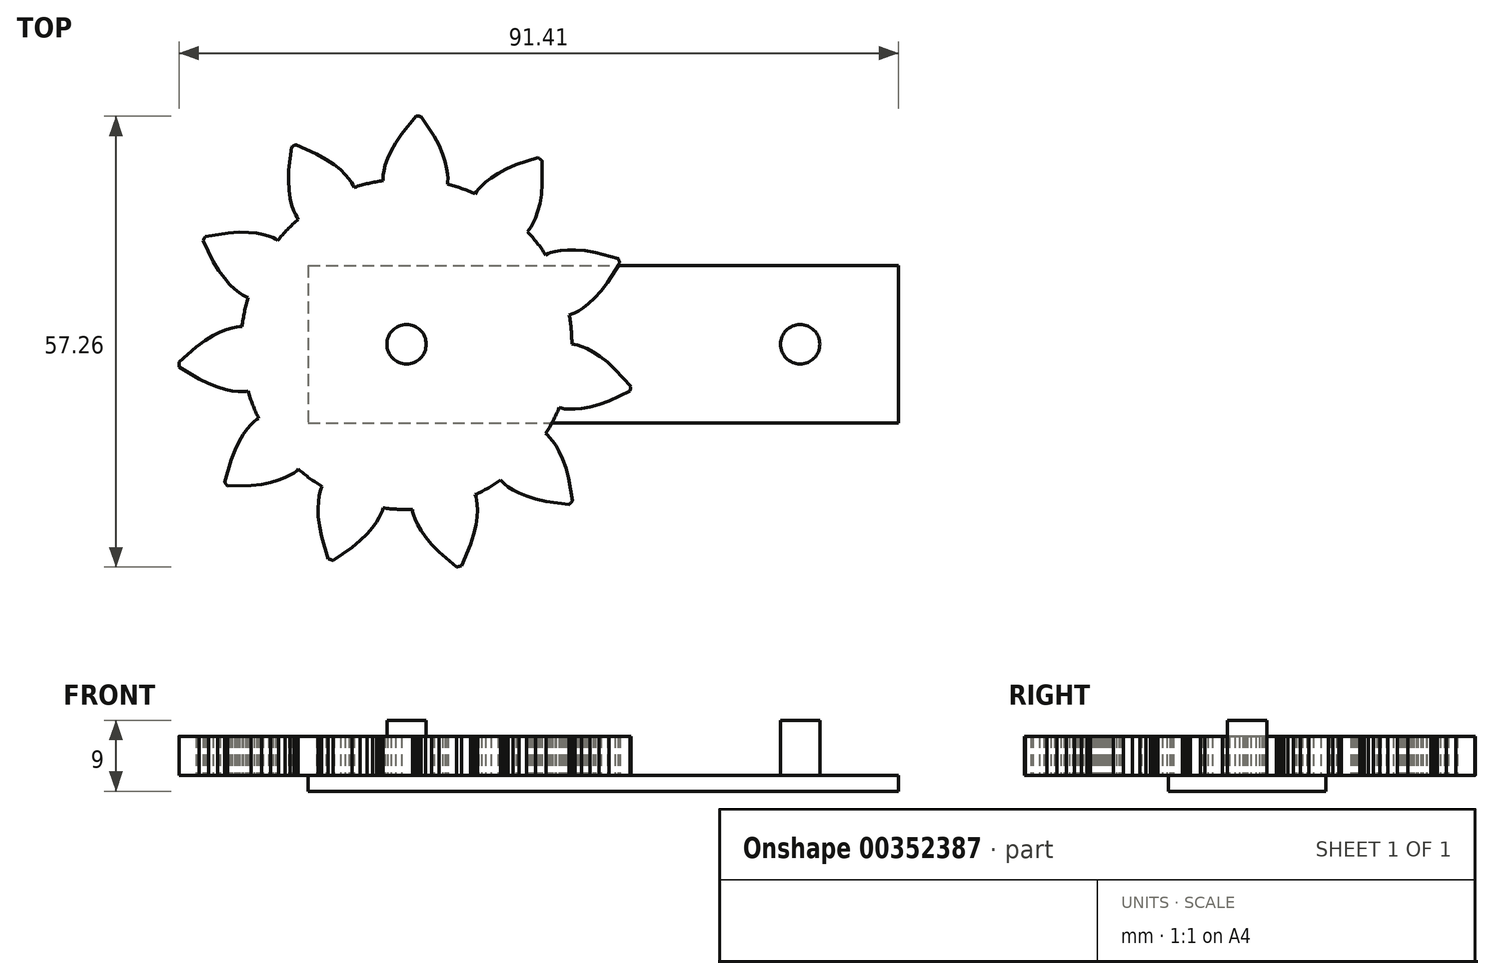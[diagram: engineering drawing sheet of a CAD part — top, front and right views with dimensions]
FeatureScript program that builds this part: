
annotation { "Feature Type Name" : "Feature", "Feature Type Description" : "" }
export const myFeature = defineFeature(function(context is Context, id is Id, definition is map)
    precondition{}
    {
        {
            var Q0;
            Q0=qCreatedBy(makeId("Top.planeOp"),FACE);
            var sketch = newSketch(context, id + "F0", { "sketchPlane" : qUnion([Q0])});
            skCircle(sketch, "E0", {"center": v(0, 0) * mm, "radius": 25 * mm, "construction": true});
            skCircle(sketch, "E1", {"center": v(-50, 0) * mm, "radius": 25 * mm, "construction": true});
            skCircle(sketch, "E2", {"center": v(0, 0) * mm, "radius": 21 * mm, "construction": true});
            skCircle(sketch, "E3", {"center": v(-50, 0) * mm, "radius": 21 * mm, "construction": true});
            skCircle(sketch, "E4", {"center": v(-50, 0) * mm, "radius": 29 * mm, "construction": true});
            skCircle(sketch, "E5", {"center": v(0, 0) * mm, "radius": 29 * mm, "construction": true});
            skLineSegment(sketch, "E6", {"start": v(-32.36, 11.4) * mm, "end": v(-17.64, -11.4) * mm, "construction": true});
            skLineSegment(sketch, "E7", {"start": v(-50, 0) * mm, "end": v(0, 0) * mm, "construction": true});
            skLineSegment(sketch, "E8", {"start": v(-50, 0) * mm, "end": v(-25.48, 4.88) * mm, "construction": true});
            skSolve(sketch);
        }
        {
            var Q0;
            Q0=qCreatedBy(makeId("Top.planeOp"),FACE);
            var sketch = newSketch(context, id + "F1", { "sketchPlane" : qUnion([Q0])});
            skCircle(sketch, "E9.1", {"center": v(-50, 0) * mm, "radius": 25 * mm, "construction": true});
            skCircle(sketch, "E9.2", {"center": v(-50, 0) * mm, "radius": 29 * mm, "construction": true});
            skLineSegment(sketch, "E9.4", {"start": v(-50, 0) * mm, "end": v(-25.48, 4.88) * mm, "construction": true});
            skLineSegment(sketch, "E10", {"start": v(-50, 0) * mm, "end": v(-29, 0) * mm, "construction": true});
            skLineSegment(sketch, "E11.1.0", {"start": v(-50, 0) * mm, "end": v(-29.08, -1.83) * mm, "construction": true});
            skLineSegment(sketch, "E11.2.0", {"start": v(-50, 0) * mm, "end": v(-29.32, -3.65) * mm, "construction": true});
            skLineSegment(sketch, "E11.3.0", {"start": v(-50, 0) * mm, "end": v(-29.72, -5.44) * mm, "construction": true});
            skLineSegment(sketch, "E11.4.0", {"start": v(-50, 0) * mm, "end": v(-30.27, -7.18) * mm, "construction": true});
            skLineSegment(sketch, "E11.5.0", {"start": v(-50, 0) * mm, "end": v(-30.97, -8.87) * mm, "construction": true});
            skLineSegment(sketch, "E11.6.0", {"start": v(-50, 0) * mm, "end": v(-31.81, -10.5) * mm, "construction": true});
            skLineSegment(sketch, "E11.7.0", {"start": v(-50, 0) * mm, "end": v(-32.8, -12.05) * mm, "construction": true});
            skLineSegment(sketch, "E11.8.0", {"start": v(-50, 0) * mm, "end": v(-33.91, -13.5) * mm, "construction": true});
            skLineSegment(sketch, "E11.9.0", {"start": v(-50, 0) * mm, "end": v(-35.15, -14.85) * mm, "construction": true});
            skLineSegment(sketch, "E11.10.0", {"start": v(-50, 0) * mm, "end": v(-36.5, -16.09) * mm, "construction": true});
            skLineSegment(sketch, "E11.anchor2", {"start": v(-50, 0) * mm, "end": v(-36.5, -16.09) * mm, "construction": true});
            skArc(sketch, "E12", {"start": v(-29.08, -1.83) * mm, "mid": v(-29.02, -0.92) * mm, "end": v(-29, 0) * mm, "construction": true});
            skArc(sketch, "E13", {"start": v(-29, 0) * mm, "mid": v(-70.98, 0.92) * mm, "end": v(-29.08, -1.83) * mm, "construction": true});
            skLineSegment(sketch, "E14", {"start": v(-29.32, -3.65) * mm, "end": v(-28.68, -0.04) * mm, "construction": true});
            skLineSegment(sketch, "E15", {"start": v(-29.72, -5.44) * mm, "end": v(-28.3, -0.12) * mm, "construction": true});
            skLineSegment(sketch, "E16", {"start": v(-30.27, -7.18) * mm, "end": v(-27.76, -0.3) * mm, "construction": true});
            skLineSegment(sketch, "E17", {"start": v(-30.97, -8.87) * mm, "end": v(-27.1, -0.57) * mm, "construction": true});
            skLineSegment(sketch, "E18", {"start": v(-31.81, -10.5) * mm, "end": v(-26.31, -0.98) * mm, "construction": true});
            skLineSegment(sketch, "E19", {"start": v(-32.8, -12.05) * mm, "end": v(-25.44, -1.53) * mm, "construction": true});
            skLineSegment(sketch, "E20", {"start": v(-33.91, -13.5) * mm, "end": v(-24.49, -2.27) * mm, "construction": true});
            skLineSegment(sketch, "E21", {"start": v(-35.15, -14.85) * mm, "end": v(-23.49, -3.18) * mm, "construction": true});
            skLineSegment(sketch, "E22", {"start": v(-36.5, -16.09) * mm, "end": v(-22.46, -4.3) * mm, "construction": true});
            skLineSegment(sketch, "E23", {"start": v(-29, 0) * mm, "end": v(-28.68, -0.04) * mm});
            skLineSegment(sketch, "E24", {"start": v(-28.68, -0.04) * mm, "end": v(-28.3, -0.12) * mm});
            skLineSegment(sketch, "E25", {"start": v(-28.3, -0.12) * mm, "end": v(-27.76, -0.3) * mm});
            skLineSegment(sketch, "E26", {"start": v(-27.76, -0.3) * mm, "end": v(-27.1, -0.57) * mm});
            skLineSegment(sketch, "E27", {"start": v(-27.1, -0.57) * mm, "end": v(-26.31, -0.98) * mm});
            skLineSegment(sketch, "E28", {"start": v(-26.31, -0.98) * mm, "end": v(-25.44, -1.53) * mm});
            skLineSegment(sketch, "E29", {"start": v(-25.44, -1.53) * mm, "end": v(-24.49, -2.27) * mm});
            skLineSegment(sketch, "E30", {"start": v(-24.49, -2.27) * mm, "end": v(-23.49, -3.18) * mm});
            skLineSegment(sketch, "E31", {"start": v(-23.49, -3.18) * mm, "end": v(-21.5, -5.35) * mm});
            skSolve(sketch);
        }
        {
            var Q0;
            Q0=qCreatedBy(makeId("Top.planeOp"),FACE);
            var sketch = newSketch(context, id + "F2", { "sketchPlane" : qUnion([Q0])});
            skLineSegment(sketch, "E32.0", {"start": v(-50, 0) * mm, "end": v(-29, 0) * mm, "construction": true});
            skLineSegment(sketch, "E32.1", {"start": v(-29, 0) * mm, "end": v(-28.68, -0.04) * mm});
            skLineSegment(sketch, "E32.2", {"start": v(-28.68, -0.04) * mm, "end": v(-28.3, -0.12) * mm});
            skLineSegment(sketch, "E32.3", {"start": v(-28.3, -0.12) * mm, "end": v(-27.76, -0.3) * mm});
            skLineSegment(sketch, "E32.4", {"start": v(-27.76, -0.3) * mm, "end": v(-27.1, -0.57) * mm});
            skLineSegment(sketch, "E32.5", {"start": v(-27.1, -0.57) * mm, "end": v(-26.31, -0.98) * mm});
            skLineSegment(sketch, "E32.6", {"start": v(-26.31, -0.98) * mm, "end": v(-25.44, -1.53) * mm});
            skLineSegment(sketch, "E32.7", {"start": v(-25.44, -1.53) * mm, "end": v(-24.49, -2.27) * mm});
            skArc(sketch, "E32.9", {"start": v(-21.56, -5.66) * mm, "mid": v(-21.53, -5.5) * mm, "end": v(-21.5, -5.35) * mm});
            skArc(sketch, "E33.converted", {"start": v(-29, 0) * mm, "mid": v(-29.1, 2.06) * mm, "end": v(-29.4, 4.1) * mm});
            skLineSegment(sketch, "E34", {"start": v(-50, 0) * mm, "end": v(-21.56, -5.66) * mm, "construction": true});
            skLineSegment(sketch, "E35", {"start": v(-50, 0) * mm, "end": v(-21.56, 5.66) * mm, "construction": true});
            skCircle(sketch, "E36", {"center": v(-50, 0) * mm, "radius": 2.5 * mm});
            skPoint(sketch, "E37", {"position": v(-29.1, 2.06) * mm});
            skLineSegment(sketch, "E38.0", {"start": v(-23.49, -3.18) * mm, "end": v(-21.5, -5.35) * mm});
            skLineSegment(sketch, "E38.1", {"start": v(-24.49, -2.27) * mm, "end": v(-23.49, -3.18) * mm});
            skPoint(sketch, "E38.2", {"position": v(-23.99, -2.72) * mm});
            skArc(sketch, "E39.MirrorCS", {"start": v(-21.56, -5.66) * mm, "mid": v(-21.59, -5.8) * mm, "end": v(-21.62, -5.96) * mm});
            skLineSegment(sketch, "E40.MirrorCS", {"start": v(-24.29, -7.2) * mm, "end": v(-21.62, -5.96) * mm});
            skLineSegment(sketch, "E41.MirrorCS", {"start": v(-25.56, -7.67) * mm, "end": v(-24.29, -7.2) * mm});
            skLineSegment(sketch, "E42.MirrorCS", {"start": v(-26.72, -7.98) * mm, "end": v(-25.56, -7.67) * mm});
            skLineSegment(sketch, "E43.MirrorCS", {"start": v(-27.74, -8.16) * mm, "end": v(-26.72, -7.98) * mm});
            skLineSegment(sketch, "E44.MirrorCS", {"start": v(-29.34, -8.24) * mm, "end": v(-28.62, -8.24) * mm});
            skLineSegment(sketch, "E45.MirrorCS", {"start": v(-28.62, -8.24) * mm, "end": v(-27.74, -8.16) * mm});
            skLineSegment(sketch, "E46.MirrorCS", {"start": v(-29.9, -8.2) * mm, "end": v(-29.34, -8.24) * mm});
            skLineSegment(sketch, "E47.MirrorCS", {"start": v(-30.3, -8.12) * mm, "end": v(-29.9, -8.2) * mm});
            skLineSegment(sketch, "E48.MirrorCS", {"start": v(-30.6, -8.04) * mm, "end": v(-30.3, -8.12) * mm});
            skArc(sketch, "E49.MirrorCS", {"start": v(-30.6, -8.04) * mm, "mid": v(-31.48, -9.9) * mm, "end": v(-32.54, -11.67) * mm});
            skArc(sketch, "E50.1.0", {"start": v(-29.33, 3.73) * mm, "mid": v(-29.07, 1.69) * mm, "end": v(-29, -0.37) * mm});
            skArc(sketch, "E50.1.1", {"start": v(-32.33, 11.35) * mm, "mid": v(-33.53, 13.03) * mm, "end": v(-34.89, 14.58) * mm});
            skLineSegment(sketch, "E50.1.2", {"start": v(-32.33, 11.35) * mm, "end": v(-32.05, 11.5) * mm});
            skLineSegment(sketch, "E50.1.3", {"start": v(-32.05, 11.5) * mm, "end": v(-31.67, 11.63) * mm});
            skLineSegment(sketch, "E50.1.4", {"start": v(-31.67, 11.63) * mm, "end": v(-31.13, 11.78) * mm});
            skLineSegment(sketch, "E50.1.5", {"start": v(-31.13, 11.78) * mm, "end": v(-30.42, 11.9) * mm});
            skLineSegment(sketch, "E50.1.6", {"start": v(-30.42, 11.9) * mm, "end": v(-29.55, 11.98) * mm});
            skLineSegment(sketch, "E50.1.7", {"start": v(-29.55, 11.98) * mm, "end": v(-28.5, 11.99) * mm});
            skLineSegment(sketch, "E50.1.8", {"start": v(-28.5, 11.99) * mm, "end": v(-27.31, 11.89) * mm});
            skLineSegment(sketch, "E50.1.9", {"start": v(-27.31, 11.89) * mm, "end": v(-25.97, 11.66) * mm});
            skLineSegment(sketch, "E50.1.10", {"start": v(-25.97, 11.66) * mm, "end": v(-23.13, 10.9) * mm});
            skArc(sketch, "E50.1.11", {"start": v(-23.01, 10.62) * mm, "mid": v(-23.07, 10.76) * mm, "end": v(-23.13, 10.9) * mm});
            skArc(sketch, "E50.1.12", {"start": v(-23.01, 10.62) * mm, "mid": v(-22.96, 10.47) * mm, "end": v(-22.9, 10.33) * mm});
            skLineSegment(sketch, "E50.1.13", {"start": v(-24.47, 7.84) * mm, "end": v(-22.9, 10.33) * mm});
            skLineSegment(sketch, "E50.1.14", {"start": v(-25.3, 6.76) * mm, "end": v(-24.47, 7.84) * mm});
            skLineSegment(sketch, "E50.1.15", {"start": v(-26.1, 5.87) * mm, "end": v(-25.3, 6.76) * mm});
            skLineSegment(sketch, "E50.1.16", {"start": v(-26.86, 5.17) * mm, "end": v(-26.1, 5.87) * mm});
            skLineSegment(sketch, "E50.1.17", {"start": v(-27.56, 4.63) * mm, "end": v(-26.86, 5.17) * mm});
            skLineSegment(sketch, "E50.1.18", {"start": v(-28.16, 4.24) * mm, "end": v(-27.56, 4.63) * mm});
            skLineSegment(sketch, "E50.1.19", {"start": v(-28.66, 3.98) * mm, "end": v(-28.16, 4.24) * mm});
            skLineSegment(sketch, "E50.1.20", {"start": v(-29.03, 3.82) * mm, "end": v(-28.66, 3.98) * mm});
            skLineSegment(sketch, "E50.1.21", {"start": v(-29.33, 3.73) * mm, "end": v(-29.03, 3.82) * mm});
            skArc(sketch, "E50.2.0", {"start": v(-34.63, 14.3) * mm, "mid": v(-33.3, 12.73) * mm, "end": v(-32.13, 11.04) * mm});
            skArc(sketch, "E50.2.1", {"start": v(-41.28, 19.1) * mm, "mid": v(-43.2, 19.87) * mm, "end": v(-45.17, 20.44) * mm});
            skLineSegment(sketch, "E50.2.2", {"start": v(-41.28, 19.1) * mm, "end": v(-41.11, 19.38) * mm});
            skLineSegment(sketch, "E50.2.3", {"start": v(-41.11, 19.38) * mm, "end": v(-40.87, 19.7) * mm});
            skLineSegment(sketch, "E50.2.4", {"start": v(-40.87, 19.7) * mm, "end": v(-40.5, 20.1) * mm});
            skLineSegment(sketch, "E50.2.5", {"start": v(-40.5, 20.1) * mm, "end": v(-39.97, 20.6) * mm});
            skLineSegment(sketch, "E50.2.6", {"start": v(-39.97, 20.6) * mm, "end": v(-39.27, 21.14) * mm});
            skLineSegment(sketch, "E50.2.7", {"start": v(-39.27, 21.14) * mm, "end": v(-38.4, 21.7) * mm});
            skLineSegment(sketch, "E50.2.8", {"start": v(-38.4, 21.7) * mm, "end": v(-37.34, 22.27) * mm});
            skLineSegment(sketch, "E50.2.9", {"start": v(-37.34, 22.27) * mm, "end": v(-36.09, 22.8) * mm});
            skLineSegment(sketch, "E50.2.10", {"start": v(-36.09, 22.8) * mm, "end": v(-33.29, 23.7) * mm});
            skArc(sketch, "E50.2.11", {"start": v(-33.04, 23.52) * mm, "mid": v(-33.16, 23.61) * mm, "end": v(-33.29, 23.7) * mm});
            skArc(sketch, "E50.2.12", {"start": v(-33.04, 23.52) * mm, "mid": v(-32.91, 23.43) * mm, "end": v(-32.79, 23.34) * mm});
            skLineSegment(sketch, "E50.2.13", {"start": v(-32.76, 20.4) * mm, "end": v(-32.79, 23.34) * mm});
            skLineSegment(sketch, "E50.2.14", {"start": v(-32.87, 19.04) * mm, "end": v(-32.76, 20.4) * mm});
            skLineSegment(sketch, "E50.2.15", {"start": v(-33.07, 17.86) * mm, "end": v(-32.87, 19.04) * mm});
            skLineSegment(sketch, "E50.2.16", {"start": v(-33.33, 16.85) * mm, "end": v(-33.07, 17.86) * mm});
            skLineSegment(sketch, "E50.2.17", {"start": v(-33.62, 16.02) * mm, "end": v(-33.33, 16.85) * mm});
            skLineSegment(sketch, "E50.2.18", {"start": v(-33.92, 15.37) * mm, "end": v(-33.62, 16.02) * mm});
            skLineSegment(sketch, "E50.2.19", {"start": v(-34.2, 14.88) * mm, "end": v(-33.92, 15.37) * mm});
            skLineSegment(sketch, "E50.2.20", {"start": v(-34.42, 14.55) * mm, "end": v(-34.2, 14.88) * mm});
            skLineSegment(sketch, "E50.2.21", {"start": v(-34.63, 14.3) * mm, "end": v(-34.42, 14.55) * mm});
            skArc(sketch, "E50.3.0", {"start": v(-44.8, 20.35) * mm, "mid": v(-42.84, 19.74) * mm, "end": v(-40.94, 18.94) * mm});
            skArc(sketch, "E50.3.1", {"start": v(-52.99, 20.79) * mm, "mid": v(-55.01, 20.4) * mm, "end": v(-56.99, 19.8) * mm});
            skLineSegment(sketch, "E50.3.2", {"start": v(-52.99, 20.79) * mm, "end": v(-53, 21.1) * mm});
            skLineSegment(sketch, "E50.3.3", {"start": v(-53, 21.1) * mm, "end": v(-52.97, 21.5) * mm});
            skLineSegment(sketch, "E50.3.4", {"start": v(-52.97, 21.5) * mm, "end": v(-52.88, 22.06) * mm});
            skLineSegment(sketch, "E50.3.5", {"start": v(-52.88, 22.06) * mm, "end": v(-52.7, 22.75) * mm});
            skLineSegment(sketch, "E50.3.6", {"start": v(-52.7, 22.75) * mm, "end": v(-52.4, 23.58) * mm});
            skLineSegment(sketch, "E50.3.7", {"start": v(-52.4, 23.58) * mm, "end": v(-51.98, 24.53) * mm});
            skLineSegment(sketch, "E50.3.8", {"start": v(-51.98, 24.53) * mm, "end": v(-51.39, 25.58) * mm});
            skLineSegment(sketch, "E50.3.9", {"start": v(-51.39, 25.58) * mm, "end": v(-50.62, 26.7) * mm});
            skLineSegment(sketch, "E50.3.10", {"start": v(-50.62, 26.7) * mm, "end": v(-48.76, 28.97) * mm});
            skArc(sketch, "E50.3.11", {"start": v(-48.45, 28.96) * mm, "mid": v(-48.6, 28.97) * mm, "end": v(-48.76, 28.97) * mm});
            skArc(sketch, "E50.3.12", {"start": v(-48.45, 28.96) * mm, "mid": v(-48.3, 28.95) * mm, "end": v(-48.14, 28.94) * mm});
            skLineSegment(sketch, "E50.3.13", {"start": v(-46.53, 26.48) * mm, "end": v(-48.14, 28.94) * mm});
            skLineSegment(sketch, "E50.3.14", {"start": v(-45.89, 25.28) * mm, "end": v(-46.53, 26.48) * mm});
            skLineSegment(sketch, "E50.3.15", {"start": v(-45.41, 24.18) * mm, "end": v(-45.89, 25.28) * mm});
            skLineSegment(sketch, "E50.3.16", {"start": v(-45.09, 23.2) * mm, "end": v(-45.41, 24.18) * mm});
            skLineSegment(sketch, "E50.3.17", {"start": v(-44.89, 22.33) * mm, "end": v(-45.09, 23.2) * mm});
            skLineSegment(sketch, "E50.3.18", {"start": v(-44.78, 21.62) * mm, "end": v(-44.89, 22.33) * mm});
            skLineSegment(sketch, "E50.3.19", {"start": v(-44.75, 21.06) * mm, "end": v(-44.78, 21.62) * mm});
            skLineSegment(sketch, "E50.3.20", {"start": v(-44.76, 20.66) * mm, "end": v(-44.75, 21.06) * mm});
            skLineSegment(sketch, "E50.3.21", {"start": v(-44.8, 20.35) * mm, "end": v(-44.76, 20.66) * mm});
            skArc(sketch, "E50.4.0", {"start": v(-56.63, 19.93) * mm, "mid": v(-54.65, 20.48) * mm, "end": v(-52.62, 20.84) * mm});
            skArc(sketch, "E50.4.1", {"start": v(-63.75, 15.87) * mm, "mid": v(-65.24, 14.45) * mm, "end": v(-66.58, 12.88) * mm});
            skLineSegment(sketch, "E50.4.2", {"start": v(-63.75, 15.87) * mm, "end": v(-63.93, 16.13) * mm});
            skLineSegment(sketch, "E50.4.3", {"start": v(-63.93, 16.13) * mm, "end": v(-64.12, 16.49) * mm});
            skLineSegment(sketch, "E50.4.4", {"start": v(-64.12, 16.49) * mm, "end": v(-64.34, 17) * mm});
            skLineSegment(sketch, "E50.4.5", {"start": v(-64.34, 17) * mm, "end": v(-64.57, 17.68) * mm});
            skLineSegment(sketch, "E50.4.6", {"start": v(-64.57, 17.68) * mm, "end": v(-64.77, 18.54) * mm});
            skLineSegment(sketch, "E50.4.7", {"start": v(-64.77, 18.54) * mm, "end": v(-64.92, 19.57) * mm});
            skLineSegment(sketch, "E50.4.8", {"start": v(-64.92, 19.57) * mm, "end": v(-65, 20.76) * mm});
            skLineSegment(sketch, "E50.4.9", {"start": v(-65, 20.76) * mm, "end": v(-64.96, 22.12) * mm});
            skLineSegment(sketch, "E50.4.10", {"start": v(-64.96, 22.12) * mm, "end": v(-64.62, 25.05) * mm});
            skArc(sketch, "E50.4.11", {"start": v(-64.35, 25.2) * mm, "mid": v(-64.48, 25.12) * mm, "end": v(-64.62, 25.05) * mm});
            skArc(sketch, "E50.4.12", {"start": v(-64.35, 25.2) * mm, "mid": v(-64.22, 25.28) * mm, "end": v(-64.08, 25.35) * mm});
            skLineSegment(sketch, "E50.4.13", {"start": v(-61.4, 24.15) * mm, "end": v(-64.08, 25.35) * mm});
            skLineSegment(sketch, "E50.4.14", {"start": v(-60.2, 23.5) * mm, "end": v(-61.4, 24.15) * mm});
            skLineSegment(sketch, "E50.4.15", {"start": v(-59.21, 22.82) * mm, "end": v(-60.2, 23.5) * mm});
            skLineSegment(sketch, "E50.4.16", {"start": v(-58.4, 22.17) * mm, "end": v(-59.21, 22.82) * mm});
            skLineSegment(sketch, "E50.4.17", {"start": v(-57.77, 21.55) * mm, "end": v(-58.4, 22.17) * mm});
            skLineSegment(sketch, "E50.4.18", {"start": v(-57.3, 21.01) * mm, "end": v(-57.77, 21.55) * mm});
            skLineSegment(sketch, "E50.4.19", {"start": v(-56.97, 20.56) * mm, "end": v(-57.3, 21.01) * mm});
            skLineSegment(sketch, "E50.4.20", {"start": v(-56.77, 20.22) * mm, "end": v(-56.97, 20.56) * mm});
            skLineSegment(sketch, "E50.4.21", {"start": v(-56.63, 19.93) * mm, "end": v(-56.77, 20.22) * mm});
            skArc(sketch, "E50.5.0", {"start": v(-66.35, 13.18) * mm, "mid": v(-64.98, 14.72) * mm, "end": v(-63.47, 16.11) * mm});
            skArc(sketch, "E50.5.1", {"start": v(-70.15, 5.92) * mm, "mid": v(-70.63, 3.91) * mm, "end": v(-70.92, 1.87) * mm});
            skLineSegment(sketch, "E50.5.2", {"start": v(-70.15, 5.92) * mm, "end": v(-70.44, 6.04) * mm});
            skLineSegment(sketch, "E50.5.3", {"start": v(-70.44, 6.04) * mm, "end": v(-70.8, 6.23) * mm});
            skLineSegment(sketch, "E50.5.4", {"start": v(-70.8, 6.23) * mm, "end": v(-71.26, 6.55) * mm});
            skLineSegment(sketch, "E50.5.5", {"start": v(-71.26, 6.55) * mm, "end": v(-71.82, 7) * mm});
            skLineSegment(sketch, "E50.5.6", {"start": v(-71.82, 7) * mm, "end": v(-72.45, 7.6) * mm});
            skLineSegment(sketch, "E50.5.7", {"start": v(-72.45, 7.6) * mm, "end": v(-73.13, 8.4) * mm});
            skLineSegment(sketch, "E50.5.8", {"start": v(-73.13, 8.4) * mm, "end": v(-73.84, 9.36) * mm});
            skLineSegment(sketch, "E50.5.9", {"start": v(-73.84, 9.36) * mm, "end": v(-74.54, 10.53) * mm});
            skLineSegment(sketch, "E50.5.10", {"start": v(-74.54, 10.53) * mm, "end": v(-75.84, 13.17) * mm});
            skArc(sketch, "E50.5.11", {"start": v(-75.7, 13.44) * mm, "mid": v(-75.77, 13.3) * mm, "end": v(-75.84, 13.17) * mm});
            skArc(sketch, "E50.5.12", {"start": v(-75.7, 13.44) * mm, "mid": v(-75.62, 13.58) * mm, "end": v(-75.55, 13.71) * mm});
            skLineSegment(sketch, "E50.5.13", {"start": v(-72.64, 14.16) * mm, "end": v(-75.55, 13.71) * mm});
            skLineSegment(sketch, "E50.5.14", {"start": v(-71.29, 14.24) * mm, "end": v(-72.64, 14.16) * mm});
            skLineSegment(sketch, "E50.5.15", {"start": v(-70.09, 14.22) * mm, "end": v(-71.29, 14.24) * mm});
            skLineSegment(sketch, "E50.5.16", {"start": v(-69.05, 14.1) * mm, "end": v(-70.09, 14.22) * mm});
            skLineSegment(sketch, "E50.5.17", {"start": v(-68.2, 13.93) * mm, "end": v(-69.05, 14.1) * mm});
            skLineSegment(sketch, "E50.5.18", {"start": v(-67.5, 13.73) * mm, "end": v(-68.2, 13.93) * mm});
            skLineSegment(sketch, "E50.5.19", {"start": v(-66.98, 13.52) * mm, "end": v(-67.5, 13.73) * mm});
            skLineSegment(sketch, "E50.5.20", {"start": v(-66.62, 13.35) * mm, "end": v(-66.98, 13.52) * mm});
            skLineSegment(sketch, "E50.5.21", {"start": v(-66.35, 13.18) * mm, "end": v(-66.62, 13.35) * mm});
            skArc(sketch, "E50.6.0", {"start": v(-70.88, 2.24) * mm, "mid": v(-70.56, 4.28) * mm, "end": v(-70.04, 6.28) * mm});
            skArc(sketch, "E50.6.1", {"start": v(-70.15, -5.92) * mm, "mid": v(-69.47, -7.86) * mm, "end": v(-68.6, -9.73) * mm});
            skLineSegment(sketch, "E50.6.2", {"start": v(-70.15, -5.92) * mm, "end": v(-70.46, -5.97) * mm});
            skLineSegment(sketch, "E50.6.3", {"start": v(-70.46, -5.97) * mm, "end": v(-70.86, -6) * mm});
            skLineSegment(sketch, "E50.6.4", {"start": v(-70.86, -6) * mm, "end": v(-71.42, -5.99) * mm});
            skLineSegment(sketch, "E50.6.5", {"start": v(-71.42, -5.99) * mm, "end": v(-72.14, -5.9) * mm});
            skLineSegment(sketch, "E50.6.6", {"start": v(-72.14, -5.9) * mm, "end": v(-73, -5.74) * mm});
            skLineSegment(sketch, "E50.6.7", {"start": v(-73, -5.74) * mm, "end": v(-74, -5.45) * mm});
            skLineSegment(sketch, "E50.6.8", {"start": v(-74, -5.45) * mm, "end": v(-75.12, -5.01) * mm});
            skLineSegment(sketch, "E50.6.9", {"start": v(-75.12, -5.01) * mm, "end": v(-76.34, -4.41) * mm});
            skLineSegment(sketch, "E50.6.10", {"start": v(-76.34, -4.41) * mm, "end": v(-78.86, -2.9) * mm});
            skArc(sketch, "E50.6.11", {"start": v(-78.88, -2.58) * mm, "mid": v(-78.87, -2.74) * mm, "end": v(-78.86, -2.9) * mm});
            skArc(sketch, "E50.6.12", {"start": v(-78.88, -2.58) * mm, "mid": v(-78.9, -2.43) * mm, "end": v(-78.91, -2.28) * mm});
            skLineSegment(sketch, "E50.6.13", {"start": v(-76.7, -0.33) * mm, "end": v(-78.91, -2.28) * mm});
            skLineSegment(sketch, "E50.6.14", {"start": v(-75.6, 0.47) * mm, "end": v(-76.7, -0.33) * mm});
            skLineSegment(sketch, "E50.6.15", {"start": v(-74.59, 1.1) * mm, "end": v(-75.6, 0.47) * mm});
            skLineSegment(sketch, "E50.6.16", {"start": v(-73.65, 1.56) * mm, "end": v(-74.59, 1.1) * mm});
            skLineSegment(sketch, "E50.6.17", {"start": v(-72.84, 1.88) * mm, "end": v(-73.65, 1.56) * mm});
            skLineSegment(sketch, "E50.6.18", {"start": v(-72.15, 2.09) * mm, "end": v(-72.84, 1.88) * mm});
            skLineSegment(sketch, "E50.6.19", {"start": v(-71.6, 2.2) * mm, "end": v(-72.15, 2.09) * mm});
            skLineSegment(sketch, "E50.6.20", {"start": v(-71.2, 2.24) * mm, "end": v(-71.6, 2.2) * mm});
            skLineSegment(sketch, "E50.6.21", {"start": v(-70.88, 2.24) * mm, "end": v(-71.2, 2.24) * mm});
            skArc(sketch, "E50.7.0", {"start": v(-68.78, -9.4) * mm, "mid": v(-69.6, -7.51) * mm, "end": v(-70.25, -5.56) * mm});
            skArc(sketch, "E50.7.1", {"start": v(-63.75, -15.87) * mm, "mid": v(-62.13, -17.14) * mm, "end": v(-60.4, -18.25) * mm});
            skLineSegment(sketch, "E50.7.2", {"start": v(-63.75, -15.87) * mm, "end": v(-63.99, -16.09) * mm});
            skLineSegment(sketch, "E50.7.3", {"start": v(-63.99, -16.09) * mm, "end": v(-64.3, -16.32) * mm});
            skLineSegment(sketch, "E50.7.4", {"start": v(-64.3, -16.32) * mm, "end": v(-64.79, -16.62) * mm});
            skLineSegment(sketch, "E50.7.5", {"start": v(-64.79, -16.62) * mm, "end": v(-65.43, -16.94) * mm});
            skLineSegment(sketch, "E50.7.6", {"start": v(-65.43, -16.94) * mm, "end": v(-66.25, -17.26) * mm});
            skLineSegment(sketch, "E50.7.7", {"start": v(-66.25, -17.26) * mm, "end": v(-67.24, -17.56) * mm});
            skLineSegment(sketch, "E50.7.8", {"start": v(-67.24, -17.56) * mm, "end": v(-68.42, -17.8) * mm});
            skLineSegment(sketch, "E50.7.9", {"start": v(-68.42, -17.8) * mm, "end": v(-69.77, -17.95) * mm});
            skLineSegment(sketch, "E50.7.10", {"start": v(-69.77, -17.95) * mm, "end": v(-72.71, -18.03) * mm});
            skArc(sketch, "E50.7.11", {"start": v(-72.9, -17.8) * mm, "mid": v(-72.8, -17.91) * mm, "end": v(-72.71, -18.03) * mm});
            skArc(sketch, "E50.7.12", {"start": v(-72.9, -17.8) * mm, "mid": v(-73, -17.67) * mm, "end": v(-73.09, -17.55) * mm});
            skLineSegment(sketch, "E50.7.13", {"start": v(-72.28, -14.72) * mm, "end": v(-73.09, -17.55) * mm});
            skLineSegment(sketch, "E50.7.14", {"start": v(-71.8, -13.45) * mm, "end": v(-72.28, -14.72) * mm});
            skLineSegment(sketch, "E50.7.15", {"start": v(-71.28, -12.37) * mm, "end": v(-71.8, -13.45) * mm});
            skLineSegment(sketch, "E50.7.16", {"start": v(-70.74, -11.47) * mm, "end": v(-71.28, -12.37) * mm});
            skLineSegment(sketch, "E50.7.17", {"start": v(-70.23, -10.76) * mm, "end": v(-70.74, -11.47) * mm});
            skLineSegment(sketch, "E50.7.18", {"start": v(-69.76, -10.22) * mm, "end": v(-70.23, -10.76) * mm});
            skLineSegment(sketch, "E50.7.19", {"start": v(-69.36, -9.83) * mm, "end": v(-69.76, -10.22) * mm});
            skLineSegment(sketch, "E50.7.20", {"start": v(-69.05, -9.57) * mm, "end": v(-69.36, -9.83) * mm});
            skLineSegment(sketch, "E50.7.21", {"start": v(-68.78, -9.4) * mm, "end": v(-69.05, -9.57) * mm});
            skArc(sketch, "E50.8.0", {"start": v(-60.72, -18.06) * mm, "mid": v(-62.43, -16.92) * mm, "end": v(-64.03, -15.62) * mm});
            skArc(sketch, "E50.8.1", {"start": v(-52.99, -20.79) * mm, "mid": v(-50.94, -20.98) * mm, "end": v(-48.88, -20.97) * mm});
            skLineSegment(sketch, "E50.8.2", {"start": v(-52.99, -20.79) * mm, "end": v(-53.07, -21.1) * mm});
            skLineSegment(sketch, "E50.8.3", {"start": v(-53.07, -21.1) * mm, "end": v(-53.21, -21.47) * mm});
            skLineSegment(sketch, "E50.8.4", {"start": v(-53.21, -21.47) * mm, "end": v(-53.45, -21.97) * mm});
            skLineSegment(sketch, "E50.8.5", {"start": v(-53.45, -21.97) * mm, "end": v(-53.82, -22.6) * mm});
            skLineSegment(sketch, "E50.8.6", {"start": v(-53.82, -22.6) * mm, "end": v(-54.34, -23.3) * mm});
            skLineSegment(sketch, "E50.8.7", {"start": v(-54.34, -23.3) * mm, "end": v(-55.01, -24.1) * mm});
            skLineSegment(sketch, "E50.8.8", {"start": v(-55.01, -24.1) * mm, "end": v(-55.87, -24.93) * mm});
            skLineSegment(sketch, "E50.8.9", {"start": v(-55.87, -24.93) * mm, "end": v(-56.93, -25.8) * mm});
            skLineSegment(sketch, "E50.8.10", {"start": v(-56.93, -25.8) * mm, "end": v(-59.36, -27.45) * mm});
            skArc(sketch, "E50.8.11", {"start": v(-59.65, -27.35) * mm, "mid": v(-59.5, -27.4) * mm, "end": v(-59.36, -27.45) * mm});
            skArc(sketch, "E50.8.12", {"start": v(-59.65, -27.35) * mm, "mid": v(-59.8, -27.3) * mm, "end": v(-59.94, -27.24) * mm});
            skLineSegment(sketch, "E50.8.13", {"start": v(-60.8, -24.43) * mm, "end": v(-59.94, -27.24) * mm});
            skLineSegment(sketch, "E50.8.14", {"start": v(-61.07, -23.1) * mm, "end": v(-60.8, -24.43) * mm});
            skLineSegment(sketch, "E50.8.15", {"start": v(-61.21, -21.9) * mm, "end": v(-61.07, -23.1) * mm});
            skLineSegment(sketch, "E50.8.16", {"start": v(-61.25, -20.87) * mm, "end": v(-61.21, -21.9) * mm});
            skLineSegment(sketch, "E50.8.17", {"start": v(-61.2, -19.99) * mm, "end": v(-61.25, -20.87) * mm});
            skLineSegment(sketch, "E50.8.18", {"start": v(-61.1, -19.28) * mm, "end": v(-61.2, -19.99) * mm});
            skLineSegment(sketch, "E50.8.19", {"start": v(-60.97, -18.73) * mm, "end": v(-61.1, -19.28) * mm});
            skLineSegment(sketch, "E50.8.20", {"start": v(-60.85, -18.35) * mm, "end": v(-60.97, -18.73) * mm});
            skLineSegment(sketch, "E50.8.21", {"start": v(-60.72, -18.06) * mm, "end": v(-60.85, -18.35) * mm});
            skArc(sketch, "E50.9.0", {"start": v(-49.25, -20.99) * mm, "mid": v(-51.31, -20.96) * mm, "end": v(-53.36, -20.73) * mm});
            skArc(sketch, "E50.9.1", {"start": v(-41.28, -19.1) * mm, "mid": v(-39.45, -18.16) * mm, "end": v(-37.72, -17.03) * mm});
            skLineSegment(sketch, "E50.9.2", {"start": v(-41.28, -19.1) * mm, "end": v(-41.18, -19.4) * mm});
            skLineSegment(sketch, "E50.9.3", {"start": v(-41.18, -19.4) * mm, "end": v(-41.1, -19.8) * mm});
            skLineSegment(sketch, "E50.9.4", {"start": v(-41.1, -19.8) * mm, "end": v(-41.03, -20.35) * mm});
            skLineSegment(sketch, "E50.9.5", {"start": v(-41.03, -20.35) * mm, "end": v(-41, -21.07) * mm});
            skLineSegment(sketch, "E50.9.6", {"start": v(-41, -21.07) * mm, "end": v(-41.05, -21.95) * mm});
            skLineSegment(sketch, "E50.9.7", {"start": v(-41.05, -21.95) * mm, "end": v(-41.2, -22.98) * mm});
            skLineSegment(sketch, "E50.9.8", {"start": v(-41.2, -22.98) * mm, "end": v(-41.46, -24.15) * mm});
            skLineSegment(sketch, "E50.9.9", {"start": v(-41.46, -24.15) * mm, "end": v(-41.88, -25.44) * mm});
            skLineSegment(sketch, "E50.9.10", {"start": v(-41.88, -25.44) * mm, "end": v(-43.03, -28.15) * mm});
            skArc(sketch, "E50.9.11", {"start": v(-43.33, -28.22) * mm, "mid": v(-43.18, -28.19) * mm, "end": v(-43.03, -28.15) * mm});
            skArc(sketch, "E50.9.12", {"start": v(-43.33, -28.22) * mm, "mid": v(-43.48, -28.26) * mm, "end": v(-43.63, -28.3) * mm});
            skLineSegment(sketch, "E50.9.13", {"start": v(-45.87, -26.38) * mm, "end": v(-43.63, -28.3) * mm});
            skLineSegment(sketch, "E50.9.14", {"start": v(-46.83, -25.42) * mm, "end": v(-45.87, -26.38) * mm});
            skLineSegment(sketch, "E50.9.15", {"start": v(-47.59, -24.5) * mm, "end": v(-46.83, -25.42) * mm});
            skLineSegment(sketch, "E50.9.16", {"start": v(-48.18, -23.64) * mm, "end": v(-47.59, -24.5) * mm});
            skLineSegment(sketch, "E50.9.17", {"start": v(-48.61, -22.87) * mm, "end": v(-48.18, -23.64) * mm});
            skLineSegment(sketch, "E50.9.18", {"start": v(-48.91, -22.22) * mm, "end": v(-48.61, -22.87) * mm});
            skLineSegment(sketch, "E50.9.19", {"start": v(-49.1, -21.69) * mm, "end": v(-48.91, -22.22) * mm});
            skLineSegment(sketch, "E50.9.20", {"start": v(-49.2, -21.3) * mm, "end": v(-49.1, -21.69) * mm});
            skLineSegment(sketch, "E50.9.21", {"start": v(-49.25, -20.99) * mm, "end": v(-49.2, -21.3) * mm});
            skArc(sketch, "E50.10.0", {"start": v(-38.02, -17.25) * mm, "mid": v(-39.77, -18.34) * mm, "end": v(-41.62, -19.25) * mm});
            skArc(sketch, "E50.10.1", {"start": v(-32.33, -11.35) * mm, "mid": v(-31.3, -9.57) * mm, "end": v(-30.46, -7.69) * mm});
            skLineSegment(sketch, "E50.10.2", {"start": v(-32.33, -11.35) * mm, "end": v(-32.09, -11.56) * mm});
            skLineSegment(sketch, "E50.10.3", {"start": v(-32.09, -11.56) * mm, "end": v(-31.8, -11.84) * mm});
            skLineSegment(sketch, "E50.10.4", {"start": v(-31.8, -11.84) * mm, "end": v(-31.45, -12.27) * mm});
            skLineSegment(sketch, "E50.10.5", {"start": v(-31.45, -12.27) * mm, "end": v(-31.04, -12.86) * mm});
            skLineSegment(sketch, "E50.10.6", {"start": v(-31.04, -12.86) * mm, "end": v(-30.6, -13.63) * mm});
            skLineSegment(sketch, "E50.10.7", {"start": v(-30.6, -13.63) * mm, "end": v(-30.17, -14.57) * mm});
            skLineSegment(sketch, "E50.10.8", {"start": v(-30.17, -14.57) * mm, "end": v(-29.76, -15.7) * mm});
            skLineSegment(sketch, "E50.10.9", {"start": v(-29.76, -15.7) * mm, "end": v(-29.42, -17.01) * mm});
            skLineSegment(sketch, "E50.10.10", {"start": v(-29.42, -17.01) * mm, "end": v(-28.92, -19.91) * mm});
            skArc(sketch, "E50.10.11", {"start": v(-29.13, -20.14) * mm, "mid": v(-29.02, -20.03) * mm, "end": v(-28.92, -19.91) * mm});
            skArc(sketch, "E50.10.12", {"start": v(-29.13, -20.14) * mm, "mid": v(-29.24, -20.25) * mm, "end": v(-29.35, -20.36) * mm});
            skLineSegment(sketch, "E50.10.13", {"start": v(-32.26, -19.96) * mm, "end": v(-29.35, -20.36) * mm});
            skLineSegment(sketch, "E50.10.14", {"start": v(-33.59, -19.66) * mm, "end": v(-32.26, -19.96) * mm});
            skLineSegment(sketch, "E50.10.15", {"start": v(-34.73, -19.3) * mm, "end": v(-33.59, -19.66) * mm});
            skLineSegment(sketch, "E50.10.16", {"start": v(-35.7, -18.9) * mm, "end": v(-34.73, -19.3) * mm});
            skLineSegment(sketch, "E50.10.17", {"start": v(-36.47, -18.5) * mm, "end": v(-35.7, -18.9) * mm});
            skLineSegment(sketch, "E50.10.18", {"start": v(-37.07, -18.1) * mm, "end": v(-36.47, -18.5) * mm});
            skLineSegment(sketch, "E50.10.19", {"start": v(-37.52, -17.76) * mm, "end": v(-37.07, -18.1) * mm});
            skLineSegment(sketch, "E50.10.20", {"start": v(-37.81, -17.49) * mm, "end": v(-37.52, -17.76) * mm});
            skLineSegment(sketch, "E50.10.21", {"start": v(-38.02, -17.25) * mm, "end": v(-37.81, -17.49) * mm});
            skSolve(sketch);
        }
        {
            var Q0;
            Q0=makeQuery(id+"F2.imprint","IMPRINT",FACE,{"disambiguationData":[TD([[makeQuery(id+"F2.imprint","IMPRINT",EDGE,{"derivedFrom":sQuery(id+"F2.wireOp",EDGE,"E32.1")}),-1.0]])]});
            extrude(context, id + "F3", {"entities" : qUnion([Q0]), "depth" : 5 * mm});
        }
        {
            var Q0;
            Q0=qCreatedBy(makeId("Top.planeOp"),FACE);
            var sketch = newSketch(context, id + "F4", { "sketchPlane" : qUnion([Q0])});
            skLineSegment(sketch, "E51.bottom", {"start": v(-62.5, 10) * mm, "end": v(12.5, 10) * mm});
            skLineSegment(sketch, "E51.top", {"start": v(-62.5, -10) * mm, "end": v(12.5, -10) * mm});
            skLineSegment(sketch, "E51.left", {"start": v(-62.5, 10) * mm, "end": v(-62.5, -10) * mm});
            skLineSegment(sketch, "E51.right", {"start": v(12.5, 10) * mm, "end": v(12.5, -10) * mm});
            skPoint(sketch, "E52.0", {"position": v(-25, 0) * mm});
            skCircle(sketch, "E53", {"center": v(-50, 0) * mm, "radius": 2.5 * mm});
            skCircle(sketch, "E54", {"center": v(0, 0) * mm, "radius": 2.5 * mm});
            skSolve(sketch);
        }
        {
            var Q0;
            Q0=makeQuery(id+"F4.imprint","IMPRINT",FACE,{"disambiguationData":[TD([[makeQuery(id+"F4.imprint","IMPRINT",EDGE,{"derivedFrom":sQuery(id+"F4.wireOp",EDGE,"E51.bottom")}),-1.0]])]});
            var Q1;
            Q1=makeQuery(id+"F4.imprint","IMPRINT",FACE,{"disambiguationData":[TD([[makeQuery(id+"F4.imprint","IMPRINT",EDGE,{"derivedFrom":sQuery(id+"F4.wireOp",EDGE,"E53")}),1.0]])]});
            var Q2;
            Q2=makeQuery(id+"F4.imprint","IMPRINT",FACE,{"disambiguationData":[TD([[makeQuery(id+"F4.imprint","IMPRINT",EDGE,{"derivedFrom":sQuery(id+"F4.wireOp",EDGE,"E54")}),1.0]])]});
            extrude(context, id + "F5", {"entities" : qUnion([Q0, Q1, Q2]), "oppositeDirection" : true, "depth" : 2 * mm});
        }
        {
            var Q0;
            Q0=makeQuery(id+"F4.imprint","IMPRINT",FACE,{"disambiguationData":[TD([[makeQuery(id+"F4.imprint","IMPRINT",EDGE,{"derivedFrom":sQuery(id+"F4.wireOp",EDGE,"E53")}),1.0]])]});
            var Q1;
            Q1=makeQuery(id+"F4.imprint","IMPRINT",FACE,{"disambiguationData":[TD([[makeQuery(id+"F4.imprint","IMPRINT",EDGE,{"derivedFrom":sQuery(id+"F4.wireOp",EDGE,"E54")}),1.0]])]});
            extrude(context, id + "F6", {"entities" : qUnion([Q0, Q1]), "operationType" : NewBodyOperationType.ADD, "depth" : 7 * mm});
        }
    });
